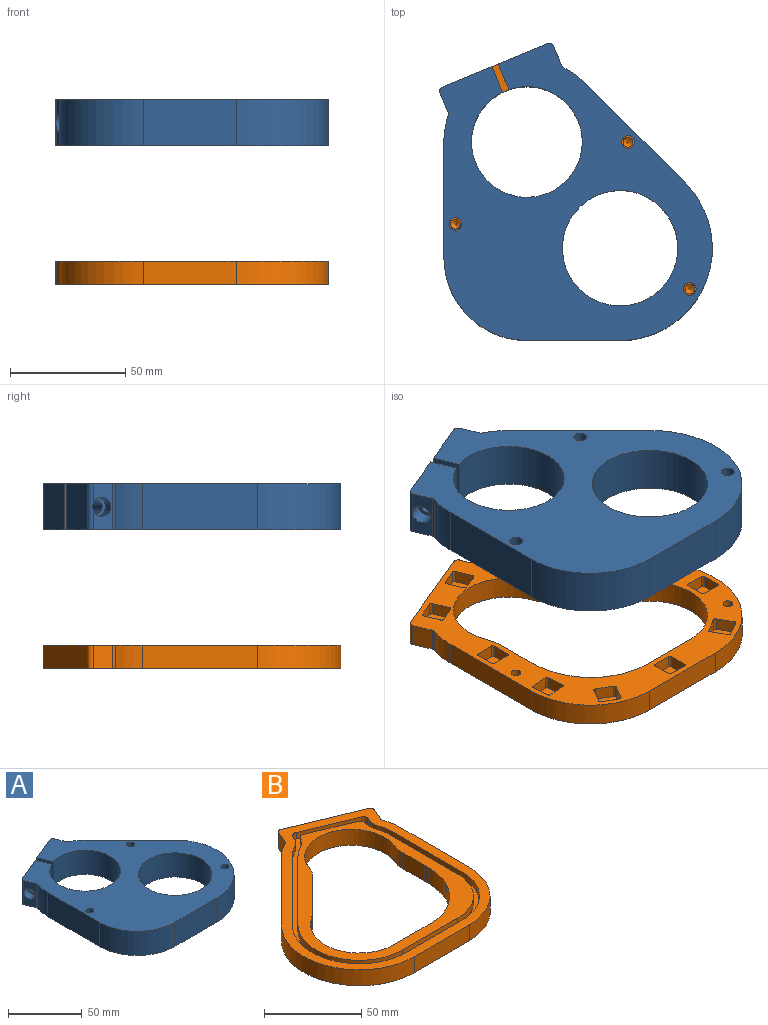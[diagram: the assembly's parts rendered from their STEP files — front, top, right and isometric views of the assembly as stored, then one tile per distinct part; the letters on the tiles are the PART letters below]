
ASSEMBLY  parts=2 mates=1
PART A: 118 faces, bbox 118.2x128.9x20 mm
  f0: plane 128.89x118.19mm, normal (0,0,-1), area 6421mm2, adj f1,f2,f3,f4,f5,f6,f7,f8
  f1: cylinder r=36mm len=20mm, axis (0,0,1), area 233.4mm2, adj f0,f2,f19,f20
  f2: plane 49.92x20mm, normal (-1,0,0), area 998.4mm2, adj f0,f1,f3,f20
  f3: cylinder r=36.16mm len=36.16mm, axis (0,0,1), area 1135.9mm2, adj f0,f2,f4,f20
  f4: plane 40.27x20mm, normal (0,-1,0), area 805.3mm2, adj f0,f3,f5,f20
  f5: cylinder r=40mm len=68.28mm, axis (0,0,1), area 1885mm2, adj f0,f4,f6,f20
  f6: plane 43.25x43.25mm, normal (0.71,0.71,0), area 1223.3mm2, adj f0,f5,f7,f20
  f7: cylinder r=36mm len=20mm, axis (0,0,1), area 233.4mm2, adj f0,f6,f8,f20
  f8: cylinder r=2mm len=20mm, axis (0,0,1), area 28.7mm2, adj f0,f7,f9,f20
  f9: plane 20x8.32mm, normal (0.92,0.38,0), area 166.1mm2, adj f0,f8,f10,f20,f21
  f10: cylinder r=2mm len=20mm, axis (0,0,1), area 62.8mm2, adj f0,f9,f11,f20
  f11: plane 21.38x20mm, normal (-0.38,0.92,0), area 462.9mm2, adj f0,f10,f12,f20
  f12: plane 20x11.1mm, normal (-0.92,-0.38,0), area 226.5mm2, adj f0,f11,f13,f20,f21
  f13: cylinder r=24mm len=48mm, axis (0,0,1), area 2955.9mm2, adj f0,f12,f14,f20
  f14: plane 20x11.1mm, normal (0.92,0.38,0), area 216.6mm2, adj f0,f13,f15,f20,f22
  f15: plane 21.38x20mm, normal (-0.38,0.92,0), area 462.9mm2, adj f0,f14,f16,f20
  f16: cylinder r=2mm len=20mm, axis (0,0,1), area 62.5mm2, adj f0,f15,f17,f20,f23
  f17: plane 20x8.32mm, normal (-0.92,-0.38,0), area 124.3mm2, adj f0,f16,f19,f20,f23
  f18: cylinder r=25mm len=50mm, axis (0,0,1), area 3141.6mm2, adj f0,f20
  f19: cylinder r=2mm len=20mm, axis (0,0,1), area 28.7mm2, adj f0,f1,f17,f20
  f20: plane 128.89x118.19mm, normal (0,0,1), area 7412.4mm2, adj f1,f2,f3,f4,f5,f6,f7,f8
  f21: cylinder r=2.1mm len=24.84mm, axis (-0.92,-0.38,0), area 331.8mm2, adj f9,f12
  f22: cylinder r=2.75mm len=19.66mm, axis (0.92,0.38,0), area 328.3mm2, adj f14,f24
  f23: cylinder r=4.22mm len=10.16mm, axis (0.92,0.38,0), area 163.1mm2, adj f16,f17,f24
  f24: plane 8.45x7.81mm, normal (-0.92,-0.38,0), area 32.3mm2, adj f22,f23
  f25: plane 5.66x5.66mm, normal (-0.71,0.71,0), area 44mm2, adj f0,f26,f32,f33
  f26: cylinder r=1mm len=5.5mm, axis (0,0,-1), area 8.6mm2, adj f0,f25,f27,f33
  f27: plane 5.66x5.66mm, normal (0.71,0.71,0), area 44mm2, adj f0,f26,f28,f33
  f28: cylinder r=1mm len=5.5mm, axis (0,0,-1), area 8.6mm2, adj f0,f27,f29,f33
  f29: plane 5.66x5.66mm, normal (0.71,-0.71,0), area 44mm2, adj f0,f28,f30,f33
  f30: cylinder r=1mm len=5.5mm, axis (0,0,-1), area 8.6mm2, adj f0,f29,f31,f33
  f31: plane 5.66x5.66mm, normal (-0.71,-0.71,0), area 44mm2, adj f0,f30,f32,f33
  f32: cylinder r=1mm len=5.5mm, axis (0,0,-1), area 8.6mm2, adj f0,f25,f31,f33
  f33: plane 13.31x13.31mm, normal (0,0,-1), area 99.1mm2, adj f25,f26,f27,f28,f29,f30,f31,f32
  f34: plane 5.66x5.66mm, normal (-0.71,0.71,0), area 44mm2, adj f0,f35,f41,f42
  f35: cylinder r=1mm len=5.5mm, axis (0,0,-1), area 8.6mm2, adj f0,f34,f36,f42
  f36: plane 5.66x5.66mm, normal (0.71,0.71,0), area 44mm2, adj f0,f35,f37,f42
  f37: cylinder r=1mm len=5.5mm, axis (0,0,-1), area 8.6mm2, adj f0,f36,f38,f42
  f38: plane 5.66x5.66mm, normal (0.71,-0.71,0), area 44mm2, adj f0,f37,f39,f42
  f39: cylinder r=1mm len=5.5mm, axis (0,0,-1), area 8.6mm2, adj f0,f38,f40,f42
  f40: plane 5.66x5.66mm, normal (-0.71,-0.71,0), area 44mm2, adj f0,f39,f41,f42
  f41: cylinder r=1mm len=5.5mm, axis (0,0,-1), area 8.6mm2, adj f0,f34,f40,f42
  f42: plane 13.31x13.31mm, normal (0,0,-1), area 99.1mm2, adj f34,f35,f36,f37,f38,f39,f40,f41
  f43: plane 7.39x5.5mm, normal (0.92,0.38,0), area 44mm2, adj f0,f44,f50,f51
  f44: cylinder r=1mm len=5.5mm, axis (0,0,-1), area 8.6mm2, adj f0,f43,f45,f51
  f45: plane 7.39x5.5mm, normal (0.38,-0.92,0), area 44mm2, adj f0,f44,f46,f51
  f46: cylinder r=1mm len=5.5mm, axis (0,0,-1), area 8.6mm2, adj f0,f45,f47,f51
  f47: plane 7.39x5.5mm, normal (-0.92,-0.38,0), area 44mm2, adj f0,f46,f48,f51
  f48: cylinder r=1mm len=5.5mm, axis (0,0,-1), area 8.6mm2, adj f0,f47,f49,f51
  f49: plane 7.39x5.5mm, normal (-0.38,0.92,0), area 44mm2, adj f0,f48,f50,f51
  f50: cylinder r=1mm len=5.5mm, axis (0,0,-1), area 8.6mm2, adj f0,f43,f49,f51
  f51: plane 12.45x12.45mm, normal (0,0,-1), area 99.1mm2, adj f43,f44,f45,f46,f47,f48,f49,f50
  f52: plane 7.39x5.5mm, normal (0.92,0.38,0), area 44mm2, adj f0,f53,f59,f60
  f53: cylinder r=1mm len=5.5mm, axis (0,0,-1), area 8.6mm2, adj f0,f52,f54,f60
  f54: plane 7.39x5.5mm, normal (0.38,-0.92,0), area 44mm2, adj f0,f53,f55,f60
  f55: cylinder r=1mm len=5.5mm, axis (0,0,-1), area 8.6mm2, adj f0,f54,f56,f60
  f56: plane 7.39x5.5mm, normal (-0.92,-0.38,0), area 44mm2, adj f0,f55,f57,f60
  f57: cylinder r=1mm len=5.5mm, axis (0,0,-1), area 8.6mm2, adj f0,f56,f58,f60
  f58: plane 7.39x5.5mm, normal (-0.38,0.92,0), area 44mm2, adj f0,f57,f59,f60
  f59: cylinder r=1mm len=5.5mm, axis (0,0,-1), area 8.6mm2, adj f0,f52,f58,f60
  f60: plane 12.45x12.45mm, normal (0,0,-1), area 99.1mm2, adj f52,f53,f54,f55,f56,f57,f58,f59
  f61: plane 8x5.5mm, normal (0,1,0), area 44mm2, adj f0,f62,f68,f69
  f62: cylinder r=1mm len=5.5mm, axis (0,0,-1), area 8.6mm2, adj f0,f61,f63,f69
  f63: plane 8x5.5mm, normal (1,0,0), area 44mm2, adj f0,f62,f64,f69
  f64: cylinder r=1mm len=5.5mm, axis (0,0,-1), area 8.6mm2, adj f0,f63,f65,f69
  f65: plane 8x5.5mm, normal (0,-1,0), area 44mm2, adj f0,f64,f66,f69
  f66: cylinder r=1mm len=5.5mm, axis (0,0,-1), area 8.6mm2, adj f0,f65,f67,f69
  f67: plane 8x5.5mm, normal (-1,0,0), area 44mm2, adj f0,f66,f68,f69
  f68: cylinder r=1mm len=5.5mm, axis (0,0,-1), area 8.6mm2, adj f0,f61,f67,f69
  f69: plane 10x10mm, normal (0,0,-1), area 99.1mm2, adj f61,f62,f63,f64,f65,f66,f67,f68
  f70: plane 8x5.5mm, normal (-1,0,0), area 44mm2, adj f0,f71,f77,f78
  f71: cylinder r=1mm len=5.5mm, axis (0,0,-1), area 8.6mm2, adj f0,f70,f72,f78
  f72: plane 8x5.5mm, normal (0,1,0), area 44mm2, adj f0,f71,f73,f78
  f73: cylinder r=1mm len=5.5mm, axis (0,0,-1), area 8.6mm2, adj f0,f72,f74,f78
  f74: plane 8x5.5mm, normal (1,0,0), area 44mm2, adj f0,f73,f75,f78
  f75: cylinder r=1mm len=5.5mm, axis (0,0,-1), area 8.6mm2, adj f0,f74,f76,f78
  f76: plane 8x5.5mm, normal (0,-1,0), area 44mm2, adj f0,f75,f77,f78
  f77: cylinder r=1mm len=5.5mm, axis (0,0,-1), area 8.6mm2, adj f0,f70,f76,f78
  f78: plane 10x10mm, normal (0,0,-1), area 99.1mm2, adj f70,f71,f72,f73,f74,f75,f76,f77
  f79: plane 7.97x5.5mm, normal (-0.09,1,0), area 44mm2, adj f0,f80,f86,f87
  f80: cylinder r=1mm len=5.5mm, axis (0,0,-1), area 8.6mm2, adj f0,f79,f81,f87
  f81: plane 7.97x5.5mm, normal (1,0.09,0), area 44mm2, adj f0,f80,f82,f87
  f82: cylinder r=1mm len=5.5mm, axis (0,0,-1), area 8.6mm2, adj f0,f81,f83,f87
  f83: plane 7.97x5.5mm, normal (0.09,-1,0), area 44mm2, adj f0,f82,f84,f87
  f84: cylinder r=1mm len=5.5mm, axis (0,0,-1), area 8.6mm2, adj f0,f83,f85,f87
  f85: plane 7.97x5.5mm, normal (-1,-0.09,0), area 44mm2, adj f0,f84,f86,f87
  f86: cylinder r=1mm len=5.5mm, axis (0,0,-1), area 8.6mm2, adj f0,f79,f85,f87
  f87: plane 10.67x10.67mm, normal (0,0,-1), area 99.1mm2, adj f79,f80,f81,f82,f83,f84,f85,f86
  f88: plane 6.93x5.5mm, normal (0.87,0.5,0), area 44mm2, adj f0,f89,f95,f96
  f89: cylinder r=1mm len=5.5mm, axis (0,0,-1), area 8.6mm2, adj f0,f88,f90,f96
  f90: plane 6.93x5.5mm, normal (0.5,-0.87,0), area 44mm2, adj f0,f89,f91,f96
  f91: cylinder r=1mm len=5.5mm, axis (0,0,-1), area 8.6mm2, adj f0,f90,f92,f96
  f92: plane 6.93x5.5mm, normal (-0.87,-0.5,0), area 44mm2, adj f0,f91,f93,f96
  f93: cylinder r=1mm len=5.5mm, axis (0,0,-1), area 8.6mm2, adj f0,f92,f94,f96
  f94: plane 6.93x5.5mm, normal (-0.5,0.87,0), area 44mm2, adj f0,f93,f95,f96
  f95: cylinder r=1mm len=5.5mm, axis (0,0,-1), area 8.6mm2, adj f0,f88,f94,f96
  f96: plane 12.93x12.93mm, normal (0,0,-1), area 99.1mm2, adj f88,f89,f90,f91,f92,f93,f94,f95
  f97: plane 6.93x5.5mm, normal (-0.87,0.5,0), area 44mm2, adj f0,f98,f104,f105
  f98: cylinder r=1mm len=5.5mm, axis (0,0,-1), area 8.6mm2, adj f0,f97,f99,f105
  f99: plane 6.93x5.5mm, normal (0.5,0.87,0), area 44mm2, adj f0,f98,f100,f105
  f100: cylinder r=1mm len=5.5mm, axis (0,0,-1), area 8.6mm2, adj f0,f99,f101,f105
  f101: plane 6.93x5.5mm, normal (0.87,-0.5,0), area 44mm2, adj f0,f100,f102,f105
  f102: cylinder r=1mm len=5.5mm, axis (0,0,-1), area 8.6mm2, adj f0,f101,f103,f105
  f103: plane 6.93x5.5mm, normal (-0.5,-0.87,0), area 44mm2, adj f0,f102,f104,f105
  f104: cylinder r=1mm len=5.5mm, axis (0,0,-1), area 8.6mm2, adj f0,f97,f103,f105
  f105: plane 12.93x12.93mm, normal (0,0,-1), area 99.1mm2, adj f97,f98,f99,f100,f101,f102,f103,f104
  f106: plane 8x5.5mm, normal (0,1,0), area 44mm2, adj f0,f107,f113,f114
  f107: cylinder r=1mm len=5.5mm, axis (0,0,-1), area 8.6mm2, adj f0,f106,f108,f114
  f108: plane 8x5.5mm, normal (1,0,0), area 44mm2, adj f0,f107,f109,f114
  f109: cylinder r=1mm len=5.5mm, axis (0,0,-1), area 8.6mm2, adj f0,f108,f110,f114
  f110: plane 8x5.5mm, normal (0,-1,0), area 44mm2, adj f0,f109,f111,f114
  f111: cylinder r=1mm len=5.5mm, axis (0,0,-1), area 8.6mm2, adj f0,f110,f112,f114
  f112: plane 8x5.5mm, normal (-1,0,0), area 44mm2, adj f0,f111,f113,f114
  f113: cylinder r=1mm len=5.5mm, axis (0,0,-1), area 8.6mm2, adj f0,f106,f112,f114
  f114: plane 10x10mm, normal (0,0,-1), area 99.1mm2, adj f106,f107,f108,f109,f110,f111,f112,f113
  f115: cylinder r=2.75mm len=20mm, axis (0,0,1), area 345.6mm2, adj f0,f20
  f116: cylinder r=2.75mm len=20mm, axis (0,0,1), area 345.6mm2, adj f0,f20
  f117: cylinder r=2.75mm len=20mm, axis (0,0,1), area 345.6mm2, adj f0,f20
PART B: 151 faces, bbox 118.2x128.9x10 mm
  f0: plane 128.89x118.19mm, normal (0,0,1), area 2115.6mm2, adj f2,f3,f4,f5,f6,f7,f8,f9
  f1: plane 128.89x118.19mm, normal (0,0,-1), area 4259.5mm2, adj f2,f3,f4,f5,f6,f7,f8,f9
  f2: plane 10x8.32mm, normal (-0.92,0.38,0), area 90mm2, adj f0,f1,f3,f26
  f3: cylinder r=2mm len=10mm, axis (0,0,1), area 31.4mm2, adj f0,f1,f2,f4
  f4: plane 45.54x18.86mm, normal (0.38,0.92,0), area 492.9mm2, adj f0,f1,f3,f5
  f5: cylinder r=2mm len=10mm, axis (0,0,1), area 31.4mm2, adj f0,f1,f4,f6
  f6: plane 10x8.32mm, normal (0.92,-0.38,0), area 90mm2, adj f0,f1,f5,f7
  f7: cylinder r=2mm len=10mm, axis (0,0,1), area 14.3mm2, adj f0,f1,f6,f8
  f8: cylinder r=36mm len=11.47mm, axis (0,0,1), area 116.7mm2, adj f0,f1,f7,f9
  f9: plane 49.92x10mm, normal (1,0,0), area 499.2mm2, adj f0,f1,f8,f10
  f10: cylinder r=36.16mm len=36.16mm, axis (0,0,1), area 567.9mm2, adj f0,f1,f9,f11
  f11: plane 40.27x10mm, normal (0,-1,0), area 402.6mm2, adj f0,f1,f10,f12
  f12: cylinder r=40mm len=68.28mm, axis (0,0,1), area 942.5mm2, adj f0,f1,f11,f13
  f13: plane 43.25x43.25mm, normal (-0.71,0.71,0), area 611.6mm2, adj f0,f1,f12,f14
  f14: cylinder r=36mm len=10mm, axis (0,0,1), area 116.7mm2, adj f0,f1,f13,f26
  f15: cylinder r=24mm len=46.8mm, axis (0,0,1), area 766.1mm2, adj f1,f16,f25,f27
  f16: cylinder r=11.9mm len=10mm, axis (0,0,1), area 55.7mm2, adj f1,f15,f17,f27
  f17: plane 23.94x23.94mm, normal (0.71,-0.71,0), area 338.5mm2, adj f1,f16,f18,f27
  f18: cylinder r=46.97mm len=10mm, axis (0,0,1), area 72.8mm2, adj f1,f17,f19,f27
  f19: cylinder r=25mm len=45.2mm, axis (0,0,1), area 627.8mm2, adj f1,f18,f20,f27
  f20: plane 26.56x10mm, normal (0,1,0), area 265.6mm2, adj f1,f19,f21,f27
  f21: cylinder r=34.55mm len=30.9mm, axis (0,0,1), area 382.5mm2, adj f1,f20,f22,f27
  f22: cylinder r=37.17mm len=17.15mm, axis (0,0,1), area 177.6mm2, adj f1,f21,f23,f27
  f23: cylinder r=185.9mm len=10mm, axis (0,0,1), area 26.5mm2, adj f1,f22,f24,f27
  f24: plane 15.71x10mm, normal (-1,0,0), area 157.1mm2, adj f1,f23,f25,f27
  f25: cylinder r=21.83mm len=10mm, axis (0,0,1), area 80.3mm2, adj f1,f15,f24,f27
  f26: cylinder r=2mm len=10mm, axis (0,0,1), area 14.3mm2, adj f0,f1,f2,f14
  f27: plane 108.98x99.42mm, normal (0,0,1), area 2115.2mm2, adj f15,f16,f17,f18,f19,f20,f21,f22
  f28: plane 7.39x5.5mm, normal (0.38,0.92,0), area 44mm2, adj f1,f29,f35,f36
  f29: cylinder r=1mm len=5.5mm, axis (0,0,-1), area 8.6mm2, adj f1,f28,f30,f36
  f30: plane 7.39x5.5mm, normal (-0.92,0.38,0), area 44mm2, adj f1,f29,f31,f36
  f31: cylinder r=1mm len=5.5mm, axis (0,0,-1), area 8.6mm2, adj f1,f30,f32,f36
  f32: plane 7.39x5.5mm, normal (-0.38,-0.92,0), area 44mm2, adj f1,f31,f33,f36
  f33: cylinder r=1mm len=5.5mm, axis (0,0,-1), area 8.6mm2, adj f1,f32,f34,f36
  f34: plane 7.39x5.5mm, normal (0.92,-0.38,0), area 44mm2, adj f1,f33,f35,f36
  f35: cylinder r=1mm len=5.5mm, axis (0,0,-1), area 8.6mm2, adj f1,f28,f34,f36
  f36: plane 12.45x12.45mm, normal (0,0,-1), area 99.1mm2, adj f28,f29,f30,f31,f32,f33,f34,f35
  f37: plane 7.39x5.5mm, normal (0.92,-0.38,0), area 44mm2, adj f1,f38,f44,f45
  f38: cylinder r=1mm len=5.5mm, axis (0,0,-1), area 8.6mm2, adj f1,f37,f39,f45
  f39: plane 7.39x5.5mm, normal (0.38,0.92,0), area 44mm2, adj f1,f38,f40,f45
  f40: cylinder r=1mm len=5.5mm, axis (0,0,-1), area 8.6mm2, adj f1,f39,f41,f45
  f41: plane 7.39x5.5mm, normal (-0.92,0.38,0), area 44mm2, adj f1,f40,f42,f45
  f42: cylinder r=1mm len=5.5mm, axis (0,0,-1), area 8.6mm2, adj f1,f41,f43,f45
  f43: plane 7.39x5.5mm, normal (-0.38,-0.92,0), area 44mm2, adj f1,f42,f44,f45
  f44: cylinder r=1mm len=5.5mm, axis (0,0,-1), area 8.6mm2, adj f1,f37,f43,f45
  f45: plane 12.45x12.45mm, normal (0,0,-1), area 99.1mm2, adj f37,f38,f39,f40,f41,f42,f43,f44
  f46: plane 8x5.5mm, normal (1,0,0), area 44mm2, adj f1,f47,f53,f54
  f47: cylinder r=1mm len=5.5mm, axis (0,0,-1), area 8.6mm2, adj f1,f46,f48,f54
  f48: plane 8x5.5mm, normal (0,1,0), area 44mm2, adj f1,f47,f49,f54
  f49: cylinder r=1mm len=5.5mm, axis (0,0,-1), area 8.6mm2, adj f1,f48,f50,f54
  f50: plane 8x5.5mm, normal (-1,0,0), area 44mm2, adj f1,f49,f51,f54
  f51: cylinder r=1mm len=5.5mm, axis (0,0,-1), area 8.6mm2, adj f1,f50,f52,f54
  f52: plane 8x5.5mm, normal (0,-1,0), area 44mm2, adj f1,f51,f53,f54
  f53: cylinder r=1mm len=5.5mm, axis (0,0,-1), area 8.6mm2, adj f1,f46,f52,f54
  f54: plane 10x10mm, normal (0,0,-1), area 99.1mm2, adj f46,f47,f48,f49,f50,f51,f52,f53
  f55: plane 7.97x5.5mm, normal (1,-0.09,0), area 44mm2, adj f1,f56,f62,f63
  f56: cylinder r=1mm len=5.5mm, axis (0,0,-1), area 8.6mm2, adj f1,f55,f57,f63
  f57: plane 7.97x5.5mm, normal (0.09,1,0), area 44mm2, adj f1,f56,f58,f63
  f58: cylinder r=1mm len=5.5mm, axis (0,0,-1), area 8.6mm2, adj f1,f57,f59,f63
  f59: plane 7.97x5.5mm, normal (-1,0.09,0), area 44mm2, adj f1,f58,f60,f63
  f60: cylinder r=1mm len=5.5mm, axis (0,0,-1), area 8.6mm2, adj f1,f59,f61,f63
  f61: plane 7.97x5.5mm, normal (-0.09,-1,0), area 44mm2, adj f1,f60,f62,f63
  f62: cylinder r=1mm len=5.5mm, axis (0,0,-1), area 8.6mm2, adj f1,f55,f61,f63
  f63: plane 10.67x10.67mm, normal (0,0,-1), area 99.1mm2, adj f55,f56,f57,f58,f59,f60,f61,f62
  f64: plane 6.93x5.5mm, normal (0.5,-0.87,0), area 44mm2, adj f1,f65,f71,f72
  f65: cylinder r=1mm len=5.5mm, axis (0,0,-1), area 8.6mm2, adj f1,f64,f66,f72
  f66: plane 6.93x5.5mm, normal (0.87,0.5,0), area 44mm2, adj f1,f65,f67,f72
  f67: cylinder r=1mm len=5.5mm, axis (0,0,-1), area 8.6mm2, adj f1,f66,f68,f72
  f68: plane 6.93x5.5mm, normal (-0.5,0.87,0), area 44mm2, adj f1,f67,f69,f72
  f69: cylinder r=1mm len=5.5mm, axis (0,0,-1), area 8.6mm2, adj f1,f68,f70,f72
  f70: plane 6.93x5.5mm, normal (-0.87,-0.5,0), area 44mm2, adj f1,f69,f71,f72
  f71: cylinder r=1mm len=5.5mm, axis (0,0,-1), area 8.6mm2, adj f1,f64,f70,f72
  f72: plane 12.93x12.93mm, normal (0,0,-1), area 99.1mm2, adj f64,f65,f66,f67,f68,f69,f70,f71
  f73: plane 8x5.5mm, normal (1,0,0), area 44mm2, adj f1,f74,f80,f81
  f74: cylinder r=1mm len=5.5mm, axis (0,0,-1), area 8.6mm2, adj f1,f73,f75,f81
  f75: plane 8x5.5mm, normal (0,1,0), area 44mm2, adj f1,f74,f76,f81
  f76: cylinder r=1mm len=5.5mm, axis (0,0,-1), area 8.6mm2, adj f1,f75,f77,f81
  f77: plane 8x5.5mm, normal (-1,0,0), area 44mm2, adj f1,f76,f78,f81
  f78: cylinder r=1mm len=5.5mm, axis (0,0,-1), area 8.6mm2, adj f1,f77,f79,f81
  f79: plane 8x5.5mm, normal (0,-1,0), area 44mm2, adj f1,f78,f80,f81
  f80: cylinder r=1mm len=5.5mm, axis (0,0,-1), area 8.6mm2, adj f1,f73,f79,f81
  f81: plane 10x10mm, normal (0,0,-1), area 99.1mm2, adj f73,f74,f75,f76,f77,f78,f79,f80
  f82: plane 6.93x5.5mm, normal (0.87,-0.5,0), area 44mm2, adj f1,f83,f89,f90
  f83: cylinder r=1mm len=5.5mm, axis (0,0,-1), area 8.6mm2, adj f1,f82,f84,f90
  f84: plane 6.93x5.5mm, normal (0.5,0.87,0), area 44mm2, adj f1,f83,f85,f90
  f85: cylinder r=1mm len=5.5mm, axis (0,0,-1), area 8.6mm2, adj f1,f84,f86,f90
  f86: plane 6.93x5.5mm, normal (-0.87,0.5,0), area 44mm2, adj f1,f85,f87,f90
  f87: cylinder r=1mm len=5.5mm, axis (0,0,-1), area 8.6mm2, adj f1,f86,f88,f90
  f88: plane 6.93x5.5mm, normal (-0.5,-0.87,0), area 44mm2, adj f1,f87,f89,f90
  f89: cylinder r=1mm len=5.5mm, axis (0,0,-1), area 8.6mm2, adj f1,f82,f88,f90
  f90: plane 12.93x12.93mm, normal (0,0,-1), area 99.1mm2, adj f82,f83,f84,f85,f86,f87,f88,f89
  f91: plane 5.66x5.66mm, normal (0.71,-0.71,0), area 44mm2, adj f1,f92,f98,f99
  f92: cylinder r=1mm len=5.5mm, axis (0,0,-1), area 8.6mm2, adj f1,f91,f93,f99
  f93: plane 5.66x5.66mm, normal (0.71,0.71,0), area 44mm2, adj f1,f92,f94,f99
  f94: cylinder r=1mm len=5.5mm, axis (0,0,-1), area 8.6mm2, adj f1,f93,f95,f99
  f95: plane 5.66x5.66mm, normal (-0.71,0.71,0), area 44mm2, adj f1,f94,f96,f99
  f96: cylinder r=1mm len=5.5mm, axis (0,0,-1), area 8.6mm2, adj f1,f95,f97,f99
  f97: plane 5.66x5.66mm, normal (-0.71,-0.71,0), area 44mm2, adj f1,f96,f98,f99
  f98: cylinder r=1mm len=5.5mm, axis (0,0,-1), area 8.6mm2, adj f1,f91,f97,f99
  f99: plane 13.31x13.31mm, normal (0,0,-1), area 99.1mm2, adj f91,f92,f93,f94,f95,f96,f97,f98
  f100: plane 5.66x5.66mm, normal (-0.71,-0.71,0), area 44mm2, adj f1,f101,f107,f108
  f101: cylinder r=1mm len=5.5mm, axis (0,0,-1), area 8.6mm2, adj f1,f100,f102,f108
  f102: plane 5.66x5.66mm, normal (0.71,-0.71,0), area 44mm2, adj f1,f101,f103,f108
  f103: cylinder r=1mm len=5.5mm, axis (0,0,-1), area 8.6mm2, adj f1,f102,f104,f108
  f104: plane 5.66x5.66mm, normal (0.71,0.71,0), area 44mm2, adj f1,f103,f105,f108
  f105: cylinder r=1mm len=5.5mm, axis (0,0,-1), area 8.6mm2, adj f1,f104,f106,f108
  f106: plane 5.66x5.66mm, normal (-0.71,0.71,0), area 44mm2, adj f1,f105,f107,f108
  f107: cylinder r=1mm len=5.5mm, axis (0,0,-1), area 8.6mm2, adj f1,f100,f106,f108
  f108: plane 13.31x13.31mm, normal (0,0,-1), area 99.1mm2, adj f100,f101,f102,f103,f104,f105,f106,f107
  f109: plane 8x5.5mm, normal (-1,0,0), area 44mm2, adj f1,f110,f116,f117
  f110: cylinder r=1mm len=5.5mm, axis (0,0,-1), area 8.6mm2, adj f1,f109,f111,f117
  f111: plane 8x5.5mm, normal (0,-1,0), area 44mm2, adj f1,f110,f112,f117
  f112: cylinder r=1mm len=5.5mm, axis (0,0,-1), area 8.6mm2, adj f1,f111,f113,f117
  f113: plane 8x5.5mm, normal (1,0,0), area 44mm2, adj f1,f112,f114,f117
  f114: cylinder r=1mm len=5.5mm, axis (0,0,-1), area 8.6mm2, adj f1,f113,f115,f117
  f115: plane 8x5.5mm, normal (0,1,0), area 44mm2, adj f1,f114,f116,f117
  f116: cylinder r=1mm len=5.5mm, axis (0,0,-1), area 8.6mm2, adj f1,f109,f115,f117
  f117: plane 10x10mm, normal (0,0,-1), area 99.1mm2, adj f109,f110,f111,f112,f113,f114,f115,f116
  f118: plane 28x11.6mm, normal (0.38,0.92,0), area 121.2mm2, adj f27,f140,f149,f150
  f119: cylinder r=10.5mm len=5.03mm, axis (0,0,1), area 28.6mm2, adj f27,f120,f140,f149
  f120: cylinder r=27.5mm len=7.21mm, axis (0,0,1), area 35.7mm2, adj f27,f119,f121,f140
  f121: plane 43.25x43.25mm, normal (-0.71,0.71,0), area 244.7mm2, adj f27,f120,f122,f140
  f122: cylinder r=31.5mm len=53.77mm, axis (0,0,1), area 296.9mm2, adj f27,f121,f123,f140
  f123: plane 40.27x4mm, normal (0,-1,0), area 161.1mm2, adj f27,f122,f124,f140
  f124: cylinder r=27.66mm len=27.66mm, axis (0,0,1), area 173.8mm2, adj f27,f123,f125,f140
  f125: plane 49.92x4mm, normal (1,0,0), area 199.7mm2, adj f27,f124,f126,f140
  f126: cylinder r=27.5mm len=8.76mm, axis (0,0,1), area 35.7mm2, adj f27,f125,f127,f140
  f127: cylinder r=10.5mm len=7mm, axis (0,0,1), area 28.6mm2, adj f27,f126,f140,f150
  f128: plane 33.53x13.89mm, normal (-0.38,-0.92,0), area 145.2mm2, adj f0,f140,f147,f148
  f129: plane 4x2.31mm, normal (-0.92,0.38,0), area 10mm2, adj f0,f130,f140,f147
  f130: cylinder r=7.5mm len=5.26mm, axis (0,0,1), area 21.5mm2, adj f0,f129,f131,f140
  f131: cylinder r=30.5mm len=9.72mm, axis (0,0,1), area 39.6mm2, adj f0,f130,f132,f140
  f132: plane 49.92x4mm, normal (-1,0,0), area 199.7mm2, adj f0,f131,f133,f140
  f133: cylinder r=30.66mm len=30.66mm, axis (0,0,1), area 192.6mm2, adj f0,f132,f134,f140
  f134: plane 40.27x4mm, normal (0,1,0), area 161.1mm2, adj f0,f133,f135,f140
  f135: cylinder r=34.5mm len=58.9mm, axis (0,0,1), area 325.2mm2, adj f0,f134,f136,f140
  f136: plane 43.25x43.25mm, normal (0.71,-0.71,0), area 244.7mm2, adj f0,f135,f137,f140
  f137: cylinder r=30.5mm len=7.99mm, axis (0,0,1), area 39.6mm2, adj f0,f136,f138,f140
  f138: cylinder r=7.5mm len=4mm, axis (0,0,1), area 21.5mm2, adj f0,f137,f139,f140
  f139: plane 4x2.31mm, normal (0.92,-0.38,0), area 10mm2, adj f0,f138,f140,f148
  f140: plane 115.9x105.42mm, normal (0,0,1), area 1061.7mm2, adj f118,f119,f120,f121,f122,f123,f124,f125
  f141: cone r=0mm half-angle=59deg, axis (0,0,-1), area 16.2mm2, adj f142
  f142: cylinder r=2.1mm len=5mm, axis (0,0,-1), area 66mm2, adj f1,f141
  f143: cone r=0mm half-angle=59deg, axis (0,0,-1), area 16.2mm2, adj f144
  f144: cylinder r=2.1mm len=5mm, axis (0,0,-1), area 66mm2, adj f1,f143
  f145: cone r=0mm half-angle=59deg, axis (0,0,-1), area 16.2mm2, adj f146
  f146: cylinder r=2.1mm len=5mm, axis (0,0,-1), area 66mm2, adj f1,f145
  f147: cylinder r=3mm len=4mm, axis (0,0,-1), area 18.8mm2, adj f0,f128,f129,f140
  f148: cylinder r=3mm len=4mm, axis (0,0,-1), area 18.8mm2, adj f0,f128,f139,f140
  f149: cylinder r=3mm len=4mm, axis (0,0,1), area 18.4mm2, adj f27,f118,f119,f140
  f150: cylinder r=3mm len=4mm, axis (0,0,1), area 18.4mm2, adj f27,f118,f127,f140
PLACE A at identity
PLACE B rot(axis=(0,1,0),180deg) t=(41.52,-62.55,-80)mm
MATE slider B.f145 <-> A.f115  axis (0,0,1) through (-31,-35.54,-70)mm
